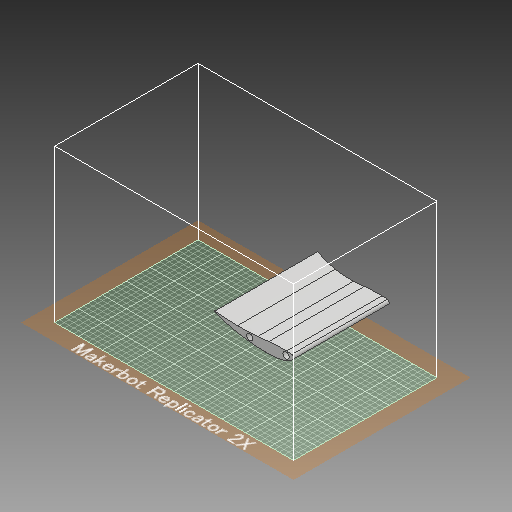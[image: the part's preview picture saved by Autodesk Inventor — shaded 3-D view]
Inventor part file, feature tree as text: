
AUTODESK INVENTOR PART (.ipt)
format: ipt  version: 2018 (Build 220112000, 112)  size: 332,288 bytes
history: native  units: mm
features: other x6, extrude x5, sketch x5, reference x4, projected_geometry x3
ambient origin geometry x8: Origin, YZ Plane, XZ Plane, XY Plane, X Axis, Y Axis, Z Axis, Center Point
bodies: Body1 (feature_tree)
feature tree (23):
  extrude  "押し出し1"  Depth=250.0mm TaperAngle=0.0deg
  other  "作業平面1"
  extrude  "押し出し4"  Depth=225.0mm TaperAngle=0.0deg
  extrude  "押し出し5"  Depth=10.0mm TaperAngle=0.0deg
  extrude  "押し出し6"  Depth=10.0mm TaperAngle=0.0deg
  extrude  "押し出し7"  Depth=41.667mm
  sketch  "スケッチ1"
  projected_geometry  "投影ループ1"
  sketch  "スケッチ4"
  reference  "参照3"
  reference  "参照4"
  sketch  "スケッチ5"
  projected_geometry  "投影ループ2"
  sketch  "スケッチ6"
  reference  "参照5"
  reference  "参照6"
  sketch  "スケッチ7"
  projected_geometry  "投影ループ3"
  other  "<userpath>\Documents\Inventor\Aero\KS-15\Fr.wing\Fr.wing_assy.iam"
  other  "Fr.wing_assy.iam"
  other  "endplate_ver2:2"
  other  "Part1:1"
  other  "newbracket2:1"
